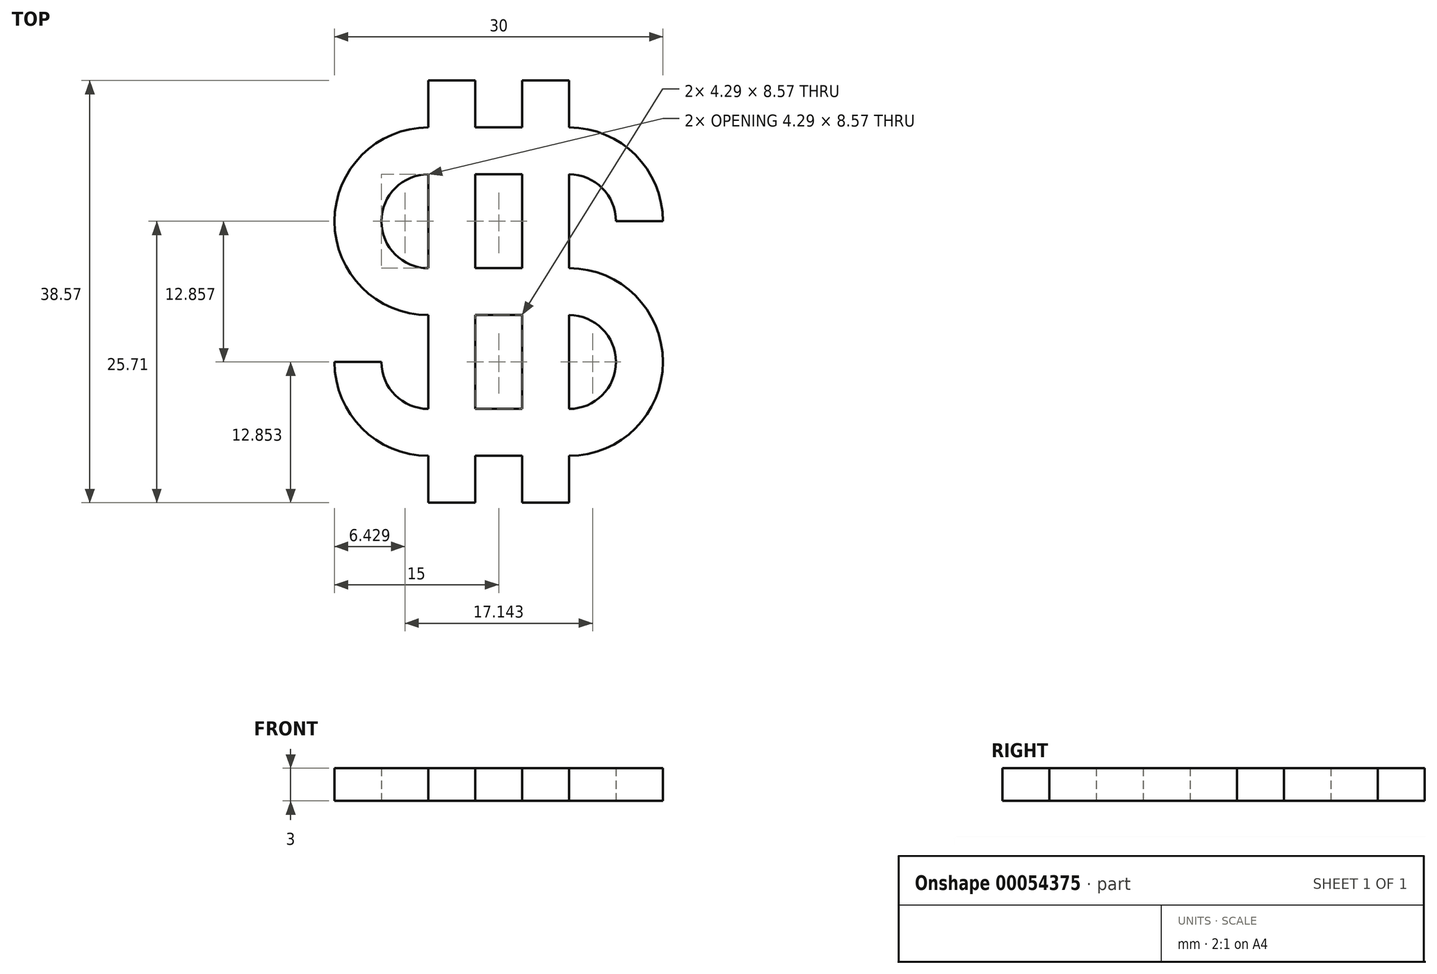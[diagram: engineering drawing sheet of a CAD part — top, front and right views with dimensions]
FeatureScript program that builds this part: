
annotation { "Feature Type Name" : "Feature", "Feature Type Description" : "" }
export const myFeature = defineFeature(function(context is Context, id is Id, definition is map)
    precondition{}
    {
        {
            var Q0;
            Q0=qCreatedBy(makeId("Top.planeOp"),FACE);
            var sketch = newSketch(context, id + "F0", { "sketchPlane" : qUnion([Q0])});
            skLineSegment(sketch, "E0", {"start": v(-4.29, 0) * mm, "end": v(0, 0) * mm});
            skArc(sketch, "E1", {"start": v(-4.29, 0) * mm, "mid": v(-5.54, 3.03) * mm, "end": v(-8.57, 4.29) * mm});
            skLineSegment(sketch, "E2", {"start": v(-8.57, 4.29) * mm, "end": v(-21.43, 4.29) * mm});
            skArc(sketch, "E3", {"start": v(-21.43, 4.29) * mm, "mid": v(-25.71, 0) * mm, "end": v(-21.43, -4.29) * mm});
            skLineSegment(sketch, "E4", {"start": v(-21.43, -4.29) * mm, "end": v(-8.57, -4.29) * mm});
            skArc(sketch, "E5", {"start": v(-8.57, -21.43) * mm, "mid": v(0, -12.86) * mm, "end": v(-8.57, -4.29) * mm});
            skLineSegment(sketch, "E6", {"start": v(-8.57, -21.43) * mm, "end": v(-21.43, -21.43) * mm});
            skLineSegment(sketch, "E7", {"start": v(0, 0) * mm, "end": v(0, -42.63) * mm, "construction": true});
            skArc(sketch, "E8", {"start": v(-30, -12.86) * mm, "mid": v(-27.49, -18.92) * mm, "end": v(-21.43, -21.43) * mm});
            skArc(sketch, "E9", {"start": v(0, 0) * mm, "mid": v(-2.51, 6.06) * mm, "end": v(-8.57, 8.57) * mm});
            skLineSegment(sketch, "E10", {"start": v(-8.57, 8.57) * mm, "end": v(-12.86, 8.57) * mm});
            skArc(sketch, "E11", {"start": v(-21.43, 8.57) * mm, "mid": v(-30, 0) * mm, "end": v(-21.43, -8.57) * mm});
            skLineSegment(sketch, "E12", {"start": v(-21.43, -8.57) * mm, "end": v(-8.57, -8.57) * mm});
            skLineSegment(sketch, "E13", {"start": v(-21.43, -8.57) * mm, "end": v(-21.43, -4.29) * mm});
            skArc(sketch, "E14", {"start": v(-8.57, -17.14) * mm, "mid": v(-4.29, -12.86) * mm, "end": v(-8.57, -8.57) * mm});
            skLineSegment(sketch, "E15", {"start": v(-8.57, -21.43) * mm, "end": v(-8.57, -17.14) * mm});
            skLineSegment(sketch, "E16", {"start": v(-8.57, -17.14) * mm, "end": v(-21.43, -17.14) * mm});
            skArc(sketch, "E17", {"start": v(-25.71, -12.86) * mm, "mid": v(-24.46, -15.89) * mm, "end": v(-21.43, -17.14) * mm});
            skLineSegment(sketch, "E18", {"start": v(-25.71, -12.86) * mm, "end": v(-30, -12.86) * mm});
            skLineSegment(sketch, "E19", {"start": v(-30, 7.94) * mm, "end": v(-30, -42.63) * mm, "construction": true});
            skPoint(sketch, "E19.startSnap0", {"position": v(-30, 0) * mm});
            skLineSegment(sketch, "E20.bottom", {"start": v(-21.43, 12.86) * mm, "end": v(-17.14, 12.86) * mm});
            skLineSegment(sketch, "E20.top", {"start": v(-21.43, -25.71) * mm, "end": v(-17.14, -25.71) * mm});
            skLineSegment(sketch, "E20.left", {"start": v(-21.43, 12.86) * mm, "end": v(-21.43, -25.71) * mm});
            skLineSegment(sketch, "E20.right", {"start": v(-17.14, 12.86) * mm, "end": v(-17.14, 8.57) * mm});
            skLineSegment(sketch, "E21.bottom", {"start": v(-8.57, 12.86) * mm, "end": v(-12.86, 12.86) * mm});
            skLineSegment(sketch, "E21.top", {"start": v(-8.57, -25.71) * mm, "end": v(-12.86, -25.71) * mm});
            skLineSegment(sketch, "E21.left", {"start": v(-8.57, 12.86) * mm, "end": v(-8.57, -25.71) * mm});
            skLineSegment(sketch, "E21.right", {"start": v(-12.86, 12.86) * mm, "end": v(-12.86, -25.71) * mm});
            skLineSegment(sketch, "E22", {"start": v(-17.14, 8.57) * mm, "end": v(-21.43, 8.57) * mm});
            skLineSegment(sketch, "E23", {"start": v(-12.86, 8.57) * mm, "end": v(-17.14, 8.57) * mm});
            skLineSegment(sketch, "E24", {"start": v(-17.14, 8.57) * mm, "end": v(-17.14, 8.57) * mm});
            skLineSegment(sketch, "E25", {"start": v(-17.14, 8.57) * mm, "end": v(-17.14, 0) * mm});
            skLineSegment(sketch, "E26", {"start": v(-17.14, -21.43) * mm, "end": v(-17.14, -25.71) * mm});
            skLineSegment(sketch, "E27", {"start": v(-17.14, -4.29) * mm, "end": v(-17.14, -21.43) * mm});
            skLineSegment(sketch, "E28", {"start": v(-17.14, 0) * mm, "end": v(-17.14, -4.29) * mm});
            skLineSegment(sketch, "E29", {"start": v(0, -42.63) * mm, "end": v(-30, -42.63) * mm, "construction": true});
            skLineSegment(sketch, "E30", {"start": v(-17.14, -4.29) * mm, "end": v(-15, -6.43) * mm, "construction": true});
            skLineSegment(sketch, "E31", {"start": v(-15, -6.43) * mm, "end": v(-12.86, -8.57) * mm, "construction": true});
            skEllipse(sketch, "E32", {"center": v(-15, -6.43) * mm, "majorRadius": 26.44 * mm, "minorRadius": 19.61 * mm, "majorAxis": v(0, 1)});
            skSolve(sketch);
        }
        {
            var Q0;
            Q0=makeQuery(id+"F0.imprint","IMPRINT",FACE,{"disambiguationData":[TD([[makeQuery(id+"F0.imprint","IMPRINT",EDGE,{"derivedFrom":sQuery(id+"F0.wireOp",EDGE,"E0")}),1.0]])]});
            var Q1;
            {var subQ5=sQuery(id+"F0.wireOp",EDGE,"E10");Q1=makeQuery(id+"F0.imprint","IMPRINT",FACE,{"disambiguationData":[TD([[makeQuery(id+"F0.imprint","IMPRINT",EDGE,{"derivedFrom":subQ5}),1.0]])]});}
            var Q2;
            {var subQ0=sQuery(id+"F0.wireOp",EDGE,"E10");Q2=makeQuery(id+"F0.imprint","IMPRINT",FACE,{"disambiguationData":[TD([[makeQuery(id+"F0.imprint","IMPRINT",EDGE,{"derivedFrom":subQ0}),-1.0]])]});}
            var Q3;
            {var subQ5=sQuery(id+"F0.wireOp",EDGE,"E23");Q3=makeQuery(id+"F0.imprint","IMPRINT",FACE,{"disambiguationData":[TD([[makeQuery(id+"F0.imprint","IMPRINT",EDGE,{"derivedFrom":subQ5}),1.0]])]});}
            var Q4;
            {var subQ1=sQuery(id+"F0.wireOp",EDGE,"E2");var subQ3=sQuery(id+"F0.wireOp",EDGE,"E21.right");var subQ4=makeQuery(id+"F0.imprint","INTERSECT",VERTEX,{"derivedFrom":[subQ1,subQ3]});Q4=makeQuery(id+"F0.imprint","IMPRINT",FACE,{"disambiguationData":[TD([[makeQuery(id+"F0.imprint","IMPRINT",EDGE,{"disambiguationData":[TD([[subQ4,-1.0]])],"derivedFrom":subQ3}),1.0]])]});}
            var Q5;
            {var subQ0=sQuery(id+"F0.wireOp",EDGE,"E28");Q5=makeQuery(id+"F0.imprint","IMPRINT",FACE,{"disambiguationData":[TD([[makeQuery(id+"F0.imprint","IMPRINT",EDGE,{"derivedFrom":subQ0}),-1.0]])]});}
            var Q6;
            {var subQ5=sQuery(id+"F0.wireOp",EDGE,"E22");Q6=makeQuery(id+"F0.imprint","IMPRINT",FACE,{"disambiguationData":[TD([[makeQuery(id+"F0.imprint","IMPRINT",EDGE,{"derivedFrom":subQ5}),1.0]])]});}
            var Q7;
            {var subQ0=sQuery(id+"F0.wireOp",EDGE,"E20.bottom");Q7=makeQuery(id+"F0.imprint","IMPRINT",FACE,{"disambiguationData":[TD([[makeQuery(id+"F0.imprint","IMPRINT",EDGE,{"derivedFrom":subQ0}),-1.0]])]});}
            extrude(context, id + "F1", {"entities" : qUnion([Q0, Q1, Q2, Q3, Q4, Q5, Q6, Q7]), "depth" : 3 * mm});
        }
        {
            var Q0;
            {var subQ0=sQuery(id+"F0.wireOp",EDGE,"E3");Q0=makeQuery(id+"F0.imprint","IMPRINT",FACE,{"disambiguationData":[TD([[makeQuery(id+"F0.imprint","IMPRINT",EDGE,{"derivedFrom":subQ0}),-1.0]])]});}
            var Q1;
            {var subQ3=sQuery(id+"F0.wireOp",EDGE,"E27");var subQ5=sQuery(id+"F0.wireOp",EDGE,"E12");var subQ7=makeQuery(id+"F0.imprint","INTERSECT",VERTEX,{"derivedFrom":[subQ5,subQ3]});Q1=makeQuery(id+"F0.imprint","IMPRINT",FACE,{"disambiguationData":[TD([[makeQuery(id+"F0.imprint","IMPRINT",EDGE,{"disambiguationData":[TD([[subQ7,1.0]])],"derivedFrom":subQ5}),1.0]])]});}
            var Q2;
            {var subQ1=sQuery(id+"F0.wireOp",EDGE,"E12");var subQ3=sQuery(id+"F0.wireOp",EDGE,"E27");var subQ4=makeQuery(id+"F0.imprint","INTERSECT",VERTEX,{"derivedFrom":[subQ1,subQ3]});Q2=makeQuery(id+"F0.imprint","IMPRINT",FACE,{"disambiguationData":[TD([[makeQuery(id+"F0.imprint","IMPRINT",EDGE,{"disambiguationData":[TD([[subQ4,-1.0]])],"derivedFrom":subQ3}),-1.0]])]});}
            var Q3;
            {var subQ0=sQuery(id+"F0.wireOp",EDGE,"E5");Q3=makeQuery(id+"F0.imprint","IMPRINT",FACE,{"disambiguationData":[TD([[makeQuery(id+"F0.imprint","IMPRINT",EDGE,{"derivedFrom":subQ0}),1.0]])]});}
            var Q4;
            {var subQ1=sQuery(id+"F0.wireOp",EDGE,"E6");var subQ3=sQuery(id+"F0.wireOp",EDGE,"E21.right");var subQ4=makeQuery(id+"F0.imprint","INTERSECT",VERTEX,{"derivedFrom":[subQ1,subQ3]});Q4=makeQuery(id+"F0.imprint","IMPRINT",FACE,{"disambiguationData":[TD([[makeQuery(id+"F0.imprint","IMPRINT",EDGE,{"disambiguationData":[TD([[subQ4,1.0]])],"derivedFrom":subQ3}),1.0]])]});}
            var Q5;
            {var subQ3=sQuery(id+"F0.wireOp",EDGE,"E21.right");var subQ5=sQuery(id+"F0.wireOp",EDGE,"E16");var subQ6=makeQuery(id+"F0.imprint","INTERSECT",VERTEX,{"derivedFrom":[subQ5,subQ3]});Q5=makeQuery(id+"F0.imprint","IMPRINT",FACE,{"disambiguationData":[TD([[makeQuery(id+"F0.imprint","IMPRINT",EDGE,{"disambiguationData":[TD([[subQ6,-1.0]])],"derivedFrom":subQ5}),1.0]])]});}
            var Q6;
            {var subQ3=sQuery(id+"F0.wireOp",EDGE,"E27");var subQ5=sQuery(id+"F0.wireOp",EDGE,"E16");var subQ6=makeQuery(id+"F0.imprint","INTERSECT",VERTEX,{"derivedFrom":[subQ5,subQ3]});Q6=makeQuery(id+"F0.imprint","IMPRINT",FACE,{"disambiguationData":[TD([[makeQuery(id+"F0.imprint","IMPRINT",EDGE,{"disambiguationData":[TD([[subQ6,-1.0]])],"derivedFrom":subQ5}),1.0]])]});}
            var Q7;
            {var subQ1=sQuery(id+"F0.wireOp",EDGE,"E4");var subQ3=sQuery(id+"F0.wireOp",EDGE,"E21.right");var subQ4=makeQuery(id+"F0.imprint","INTERSECT",VERTEX,{"derivedFrom":[subQ1,subQ3]});Q7=makeQuery(id+"F0.imprint","IMPRINT",FACE,{"disambiguationData":[TD([[makeQuery(id+"F0.imprint","IMPRINT",EDGE,{"disambiguationData":[TD([[subQ4,-1.0]])],"derivedFrom":subQ3}),1.0]])]});}
            var Q8;
            {var subQ0=sQuery(id+"F0.wireOp",EDGE,"E8");Q8=makeQuery(id+"F0.imprint","IMPRINT",FACE,{"disambiguationData":[TD([[makeQuery(id+"F0.imprint","IMPRINT",EDGE,{"derivedFrom":subQ0}),1.0]])]});}
            var Q9;
            {var subQ4=sQuery(id+"F0.wireOp",EDGE,"E20.top");Q9=makeQuery(id+"F0.imprint","IMPRINT",FACE,{"disambiguationData":[TD([[makeQuery(id+"F0.imprint","IMPRINT",EDGE,{"derivedFrom":subQ4}),1.0]])]});}
            var Q10;
            {var subQ5=sQuery(id+"F0.wireOp",EDGE,"E21.top");Q10=makeQuery(id+"F0.imprint","IMPRINT",FACE,{"disambiguationData":[TD([[makeQuery(id+"F0.imprint","IMPRINT",EDGE,{"derivedFrom":subQ5}),-1.0]])]});}
            var Q11;
            {var subQ2=sQuery(id+"F0.wireOp",EDGE,"E12");var subQ4=sQuery(id+"F0.wireOp",EDGE,"E21.right");var subQ5=makeQuery(id+"F0.imprint","INTERSECT",VERTEX,{"derivedFrom":[subQ2,subQ4]});Q11=makeQuery(id+"F0.imprint","IMPRINT",FACE,{"disambiguationData":[TD([[makeQuery(id+"F0.imprint","IMPRINT",EDGE,{"disambiguationData":[TD([[subQ5,-1.0]])],"derivedFrom":subQ4}),1.0]])]});}
            var Q12;
            {var subQ0=sQuery(id+"F0.wireOp",EDGE,"E27");var subQ5=sQuery(id+"F0.wireOp",EDGE,"E12");var subQ6=makeQuery(id+"F0.imprint","INTERSECT",VERTEX,{"derivedFrom":[subQ5,subQ0]});Q12=makeQuery(id+"F0.imprint","IMPRINT",FACE,{"disambiguationData":[TD([[makeQuery(id+"F0.imprint","IMPRINT",EDGE,{"disambiguationData":[TD([[subQ6,-1.0]])],"derivedFrom":subQ5}),1.0]])]});}
            extrude(context, id + "F2", {"entities" : qUnion([Q0, Q1, Q2, Q3, Q4, Q5, Q6, Q7, Q8, Q9, Q10, Q11, Q12]), "operationType" : NewBodyOperationType.ADD, "depth" : 3 * mm});
        }
    });
